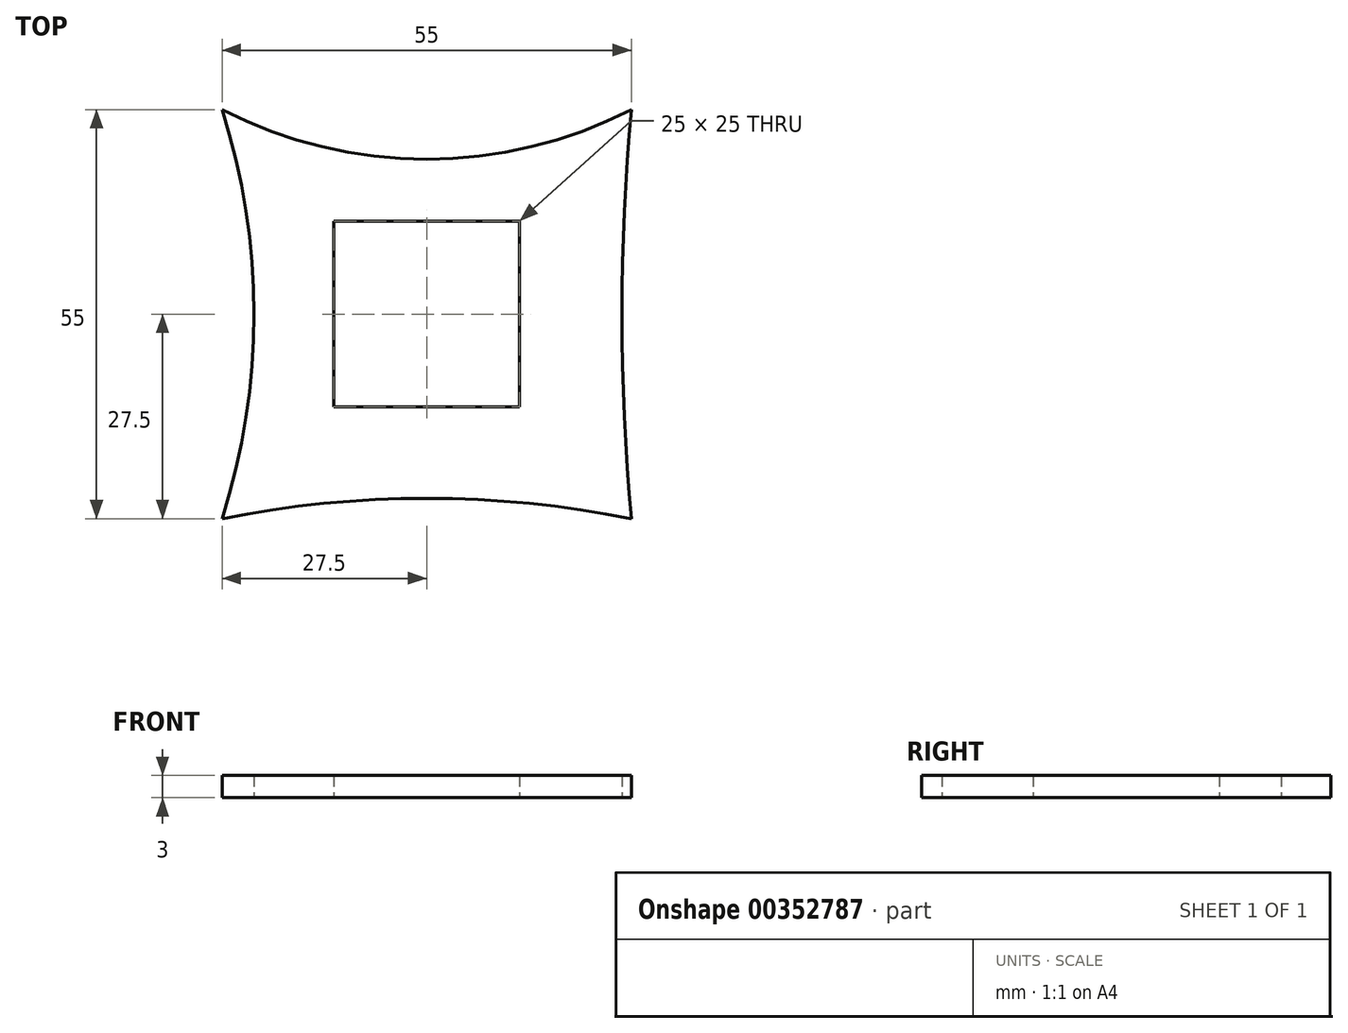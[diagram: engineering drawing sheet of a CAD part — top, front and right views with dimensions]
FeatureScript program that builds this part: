
annotation { "Feature Type Name" : "Feature", "Feature Type Description" : "" }
export const myFeature = defineFeature(function(context is Context, id is Id, definition is map)
    precondition{}
    {
        {
            var Q0;
            Q0=qCreatedBy(makeId("Top.planeOp"),FACE);
            var sketch = newSketch(context, id + "F0", { "sketchPlane" : qUnion([Q0])});
            skLineSegment(sketch, "E0.bottom", {"start": v(12.5, 12.5) * mm, "end": v(-12.5, 12.5) * mm});
            skLineSegment(sketch, "E0.top", {"start": v(12.5, -12.5) * mm, "end": v(-12.5, -12.5) * mm});
            skLineSegment(sketch, "E0.left", {"start": v(12.5, 12.5) * mm, "end": v(12.5, -12.5) * mm});
            skLineSegment(sketch, "E0.right", {"start": v(-12.5, 12.5) * mm, "end": v(-12.5, -12.5) * mm});
            skPoint(sketch, "E0.middle", {"position": v(0, 0) * mm});
            skLineSegment(sketch, "E1.bottom", {"start": v(27.5, 27.5) * mm, "end": v(-27.5, 27.5) * mm, "construction": true});
            skLineSegment(sketch, "E1.top", {"start": v(27.5, -27.5) * mm, "end": v(-27.5, -27.5) * mm, "construction": true});
            skLineSegment(sketch, "E1.left", {"start": v(27.5, 27.5) * mm, "end": v(27.5, -27.5) * mm, "construction": true});
            skLineSegment(sketch, "E1.right", {"start": v(-27.5, 27.5) * mm, "end": v(-27.5, -27.5) * mm, "construction": true});
            skArc(sketch, "E2", {"start": v(-27.5, 27.5) * mm, "mid": v(0, 20.83) * mm, "end": v(27.5, 27.5) * mm});
            skArc(sketch, "E3", {"start": v(-27.5, -27.5) * mm, "mid": v(-23.2, 0) * mm, "end": v(-27.5, 27.5) * mm});
            skArc(sketch, "E4", {"start": v(27.5, -27.5) * mm, "mid": v(0, -24.77) * mm, "end": v(-27.5, -27.5) * mm});
            skArc(sketch, "E5", {"start": v(27.5, 27.5) * mm, "mid": v(26.24, 0) * mm, "end": v(27.5, -27.5) * mm});
            skSolve(sketch);
        }
        {
            var Q0;
            Q0=makeQuery(id+"F0.imprint","IMPRINT",FACE,{"disambiguationData":[TD([[makeQuery(id+"F0.imprint","IMPRINT",EDGE,{"derivedFrom":sQuery(id+"F0.wireOp",EDGE,"E0.bottom")}),-1.0]])]});
            extrude(context, id + "F1", {"entities" : qUnion([Q0]), "depth" : 3 * mm, "offsetDistance" : 25 * mm});
        }
    });
